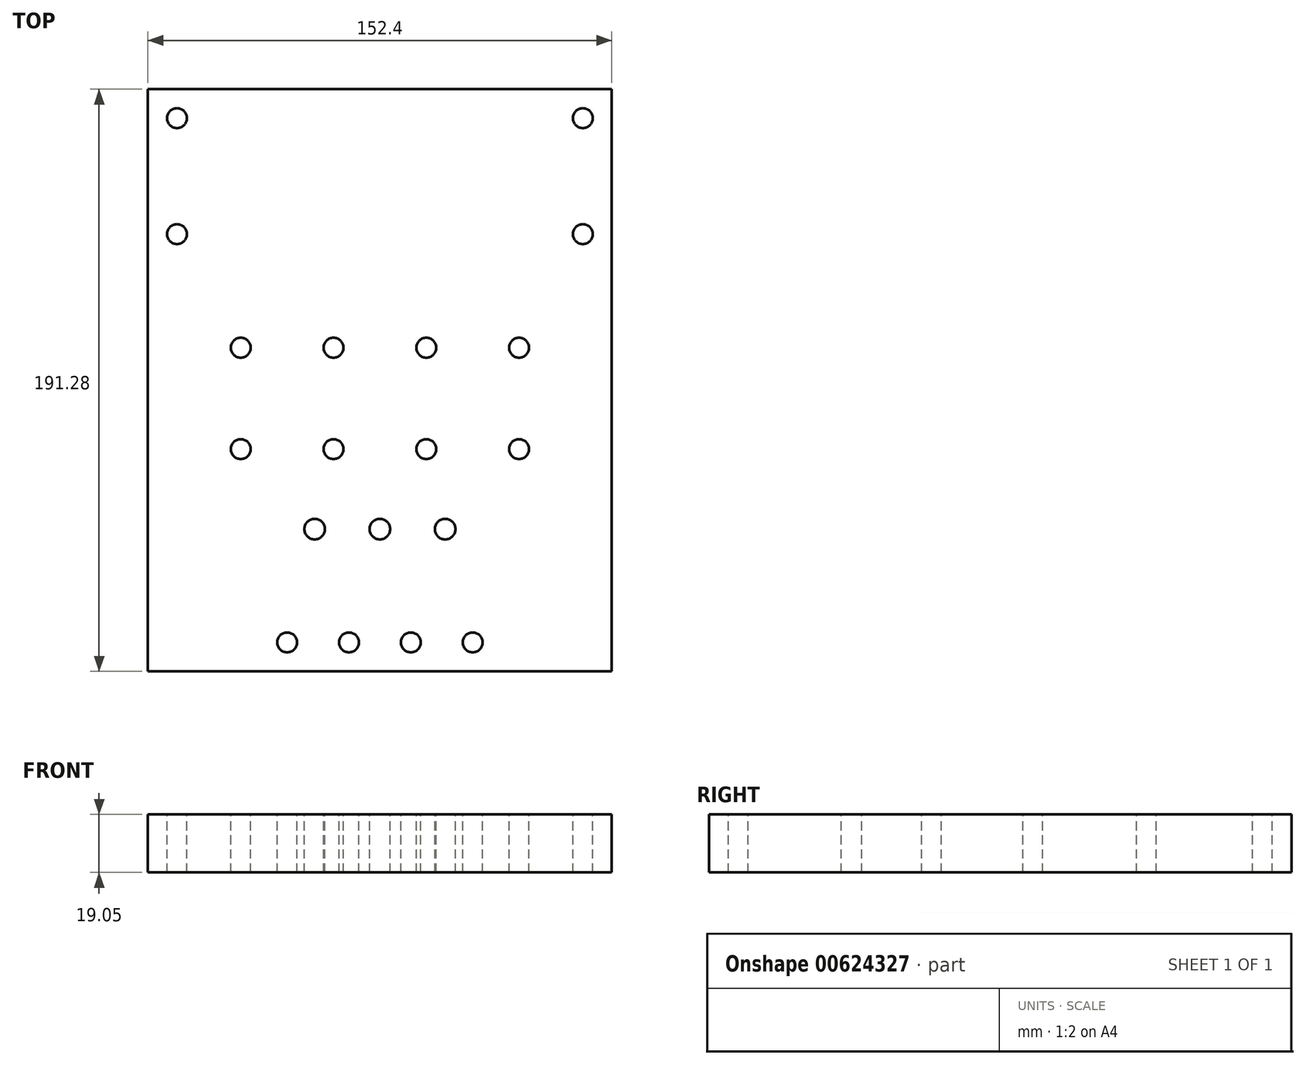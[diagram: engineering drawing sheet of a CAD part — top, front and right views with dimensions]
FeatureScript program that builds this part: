
annotation { "Feature Type Name" : "Feature", "Feature Type Description" : "" }
export const myFeature = defineFeature(function(context is Context, id is Id, definition is map)
    precondition{}
    {
        {
            var Q0;
            Q0=qCreatedBy(makeId("Top.planeOp"),FACE);
            var sketch = newSketch(context, id + "F0", { "sketchPlane" : qUnion([Q0])});
            skLineSegment(sketch, "E0.bottom", {"start": v(-76.2, 95.64) * mm, "end": v(76.2, 95.64) * mm});
            skLineSegment(sketch, "E0.top", {"start": v(-76.2, -95.64) * mm, "end": v(76.2, -95.64) * mm});
            skLineSegment(sketch, "E0.left", {"start": v(-76.2, 95.64) * mm, "end": v(-76.2, -95.64) * mm});
            skLineSegment(sketch, "E0.right", {"start": v(76.2, 95.64) * mm, "end": v(76.2, -95.64) * mm});
            skLineSegment(sketch, "E1", {"start": v(0, 95.64) * mm, "end": v(0, -95.64) * mm, "construction": true});
            skLineSegment(sketch, "E2", {"start": v(-76.2, 0) * mm, "end": v(76.2, 0) * mm, "construction": true});
            skSolve(sketch);
        }
        {
            var Q0;
            Q0=makeQuery(id+"F0.imprint","IMPRINT",FACE,{"disambiguationData":[TD([[makeQuery(id+"F0.imprint","IMPRINT",EDGE,{"derivedFrom":sQuery(id+"F0.wireOp",EDGE,"E0.bottom")}),-1.0]])]});
            extrude(context, id + "F1", {"entities" : qUnion([Q0]), "depth" : 19.05 * mm, "offsetDistance" : 25.4 * mm});
        }
        {
            var Q0;
            Q0=makeQuery(id+"F1.opExtrude","CAP_FACE",FACE,{"disambiguationData":[OSD([sQuery(id+"F0.wireOp",EDGE,"E0.bottom"),sQuery(id+"F0.wireOp",EDGE,"E0.top"),sQuery(id+"F0.wireOp",EDGE,"E0.left"),sQuery(id+"F0.wireOp",EDGE,"E0.right")])],"isStart":false});
            var sketch = newSketch(context, id + "F2", { "sketchPlane" : qUnion([Q0])});
            skLineSegment(sketch, "E3", {"start": v(-76.2, -86.11) * mm, "end": v(76.2, -86.11) * mm, "construction": true});
            skPoint(sketch, "E4", {"position": v(-30.48, -86.11) * mm});
            skPoint(sketch, "E5.1.0.0", {"position": v(-10.16, -86.11) * mm});
            skPoint(sketch, "E5.2.0.0", {"position": v(10.16, -86.11) * mm});
            skPoint(sketch, "E5.3.0.0", {"position": v(30.48, -86.11) * mm});
            skLineSegment(sketch, "E5.direction1", {"start": v(-30.48, -86.11) * mm, "end": v(-10.16, -86.11) * mm, "construction": true});
            skLineSegment(sketch, "E6", {"start": v(66.68, 95.64) * mm, "end": v(66.67, -95.64) * mm, "construction": true});
            skLineSegment(sketch, "E7", {"start": v(-66.67, 95.64) * mm, "end": v(-66.68, -95.64) * mm, "construction": true});
            skPoint(sketch, "E8", {"position": v(-66.67, 86.11) * mm});
            skPoint(sketch, "E9", {"position": v(66.68, 86.11) * mm});
            skPoint(sketch, "E10.0.1.0", {"position": v(-66.67, 48.01) * mm});
            skLineSegment(sketch, "E10.direction1", {"start": v(-66.67, 86.11) * mm, "end": v(-15.87, 86.11) * mm, "construction": true});
            skLineSegment(sketch, "E10.direction2", {"start": v(-66.67, 86.11) * mm, "end": v(-66.67, 48.01) * mm, "construction": true});
            skPoint(sketch, "E11.0.1.0", {"position": v(66.68, 48.01) * mm});
            skLineSegment(sketch, "E11.direction1", {"start": v(66.68, 86.11) * mm, "end": v(34.42, 86.11) * mm, "construction": true});
            skLineSegment(sketch, "E11.direction2", {"start": v(66.68, 86.11) * mm, "end": v(66.68, 48.01) * mm, "construction": true});
            skLineSegment(sketch, "E12", {"start": v(-76.2, -22.61) * mm, "end": v(76.2, -22.61) * mm, "construction": true});
            skPoint(sketch, "E13", {"position": v(-45.72, -22.61) * mm});
            skPoint(sketch, "E14.0.1.0", {"position": v(-45.72, 10.69) * mm});
            skPoint(sketch, "E14.1.0.0", {"position": v(-15.24, -22.61) * mm});
            skPoint(sketch, "E14.1.1.0", {"position": v(-15.24, 10.69) * mm});
            skPoint(sketch, "E14.2.0.0", {"position": v(15.24, -22.61) * mm});
            skPoint(sketch, "E14.2.1.0", {"position": v(15.24, 10.69) * mm});
            skPoint(sketch, "E14.3.0.0", {"position": v(45.72, -22.61) * mm});
            skPoint(sketch, "E14.3.1.0", {"position": v(45.72, 10.69) * mm});
            skLineSegment(sketch, "E14.direction1", {"start": v(-45.72, -22.61) * mm, "end": v(-15.24, -22.61) * mm, "construction": true});
            skLineSegment(sketch, "E14.direction2", {"start": v(-45.72, -22.61) * mm, "end": v(-45.72, 10.69) * mm, "construction": true});
            skPoint(sketch, "E15", {"position": v(0, -48.89) * mm});
            skPoint(sketch, "E16", {"position": v(21.43, -48.89) * mm});
            skPoint(sketch, "E17", {"position": v(-21.43, -48.89) * mm});
            skSolve(sketch);
        }
        {
            var Q0;
            Q0=sQuery(id+"F2.wireOp",VERTEX,"E4");
            var Q1;
            Q1=sQuery(id+"F2.wireOp",VERTEX,"E5.1.0.0");
            var Q2;
            Q2=sQuery(id+"F2.wireOp",VERTEX,"E5.2.0.0");
            var Q3;
            Q3=sQuery(id+"F2.wireOp",VERTEX,"E5.3.0.0");
            var Q4;
            Q4=sQuery(id+"F2.wireOp",VERTEX,"E10.0.1.0");
            var Q5;
            Q5=sQuery(id+"F2.wireOp",VERTEX,"E8");
            var Q6;
            Q6=sQuery(id+"F2.wireOp",VERTEX,"E9");
            var Q7;
            Q7=sQuery(id+"F2.wireOp",VERTEX,"E11.0.1.0");
            var Q8;
            Q8=sQuery(id+"F2.wireOp",VERTEX,"E14.0.1.0");
            var Q9;
            Q9=sQuery(id+"F2.wireOp",VERTEX,"E13");
            var Q10;
            Q10=sQuery(id+"F2.wireOp",VERTEX,"E14.1.0.0");
            var Q11;
            Q11=sQuery(id+"F2.wireOp",VERTEX,"E14.1.1.0");
            var Q12;
            Q12=sQuery(id+"F2.wireOp",VERTEX,"E14.2.1.0");
            var Q13;
            Q13=sQuery(id+"F2.wireOp",VERTEX,"E14.2.0.0");
            var Q14;
            Q14=sQuery(id+"F2.wireOp",VERTEX,"E14.3.0.0");
            var Q15;
            Q15=sQuery(id+"F2.wireOp",VERTEX,"E14.3.1.0");
            var Q16;
            Q16=makeQuery(id+"F1.opExtrude","SWEPT_BODY",BODY,{"disambiguationData":[OSD([sQuery(id+"F0.wireOp",EDGE,"E0.bottom"),sQuery(id+"F0.wireOp",EDGE,"E0.top"),sQuery(id+"F0.wireOp",EDGE,"E0.left"),sQuery(id+"F0.wireOp",EDGE,"E0.right")])]});
            hole(context, id + "F3", {"style" : HoleStyle.SIMPLE, "endStyle" : HoleEndStyle.THROUGH, "standardTappedOrClearance" : lookupTablePath({ "standard" : "ANSI", "fit" : "Close", "size" : "1/4", "type" : "Clearance" }), "standardBlindInLast" : lookupTablePath({ "fit" : "Close", "standard" : "ANSI", "size" : "1/4", "type" : "Clearance" }), "holeDiameter" : 6.53 * mm, "majorDiameter" : 6.35 * mm, "isTappedThrough" : true, "tappedDepth" : 12.7 * mm, "tapClearance" : 3, "startFromSketch" : true, "locations" : qUnion([Q0, Q1, Q2, Q3, Q4, Q5, Q6, Q7, Q8, Q9, Q10, Q11, Q12, Q13, Q14, Q15]), "scope" : qUnion([Q16])});
        }
        {
            var Q0;
            Q0=makeQuery(id+"F1.opExtrude","CAP_FACE",FACE,{"disambiguationData":[OSD([sQuery(id+"F0.wireOp",EDGE,"E0.bottom"),sQuery(id+"F0.wireOp",EDGE,"E0.top"),sQuery(id+"F0.wireOp",EDGE,"E0.left"),sQuery(id+"F0.wireOp",EDGE,"E0.right")])],"isStart":false});
            var sketch = newSketch(context, id + "F4", { "sketchPlane" : qUnion([Q0])});
            skLineSegment(sketch, "E18", {"start": v(-15.24, 10.69) * mm, "end": v(15.24, -22.61) * mm, "construction": true});
            skLineSegment(sketch, "E19", {"start": v(15.24, 10.69) * mm, "end": v(-15.24, -22.61) * mm, "construction": true});
            skPoint(sketch, "E20", {"position": v(0, -5.96) * mm});
            skSolve(sketch);
        }
        {
            var Q0;
            Q0=makeQuery(id+"F1.opExtrude","CAP_FACE",FACE,{"disambiguationData":[OSD([sQuery(id+"F0.wireOp",EDGE,"E0.bottom"),sQuery(id+"F0.wireOp",EDGE,"E0.top"),sQuery(id+"F0.wireOp",EDGE,"E0.left"),sQuery(id+"F0.wireOp",EDGE,"E0.right")])],"isStart":true});
            var sketch = newSketch(context, id + "F5", { "sketchPlane" : qUnion([Q0])});
            skLineSegment(sketch, "E21", {"start": v(-15.24, 22.61) * mm, "end": v(15.24, -10.69) * mm, "construction": true});
            skLineSegment(sketch, "E22", {"start": v(15.24, 22.61) * mm, "end": v(-15.24, -10.69) * mm, "construction": true});
            skPoint(sketch, "E23", {"position": v(0, 5.96) * mm});
            skSolve(sketch);
        }
        {
            var Q0;
            Q0=sQuery(id+"F2.wireOp",VERTEX,"E15");
            var Q1;
            Q1=sQuery(id+"F2.wireOp",VERTEX,"E17");
            var Q2;
            Q2=sQuery(id+"F2.wireOp",VERTEX,"E16");
            var Q3;
            Q3=makeQuery(id+"F1.opExtrude","SWEPT_BODY",BODY,{"disambiguationData":[OSD([sQuery(id+"F0.wireOp",EDGE,"E0.bottom"),sQuery(id+"F0.wireOp",EDGE,"E0.top"),sQuery(id+"F0.wireOp",EDGE,"E0.left"),sQuery(id+"F0.wireOp",EDGE,"E0.right")])]});
            hole(context, id + "F6", {"style" : HoleStyle.SIMPLE, "endStyle" : HoleEndStyle.THROUGH, "standardTappedOrClearance" : lookupTablePath({ "standard" : "ANSI", "fit" : "Normal (ASME)", "size" : "1/4", "type" : "Clearance" }), "standardBlindInLast" : lookupTablePath({ "fit" : "Free", "standard" : "ANSI", "size" : "1/4", "type" : "Clearance" }), "holeDiameter" : 6.76 * mm, "majorDiameter" : 6.35 * mm, "isTappedThrough" : true, "tappedDepth" : 12.7 * mm, "tapClearance" : 3, "startFromSketch" : true, "locations" : qUnion([Q0, Q1, Q2]), "scope" : qUnion([Q3])});
        }
    });
